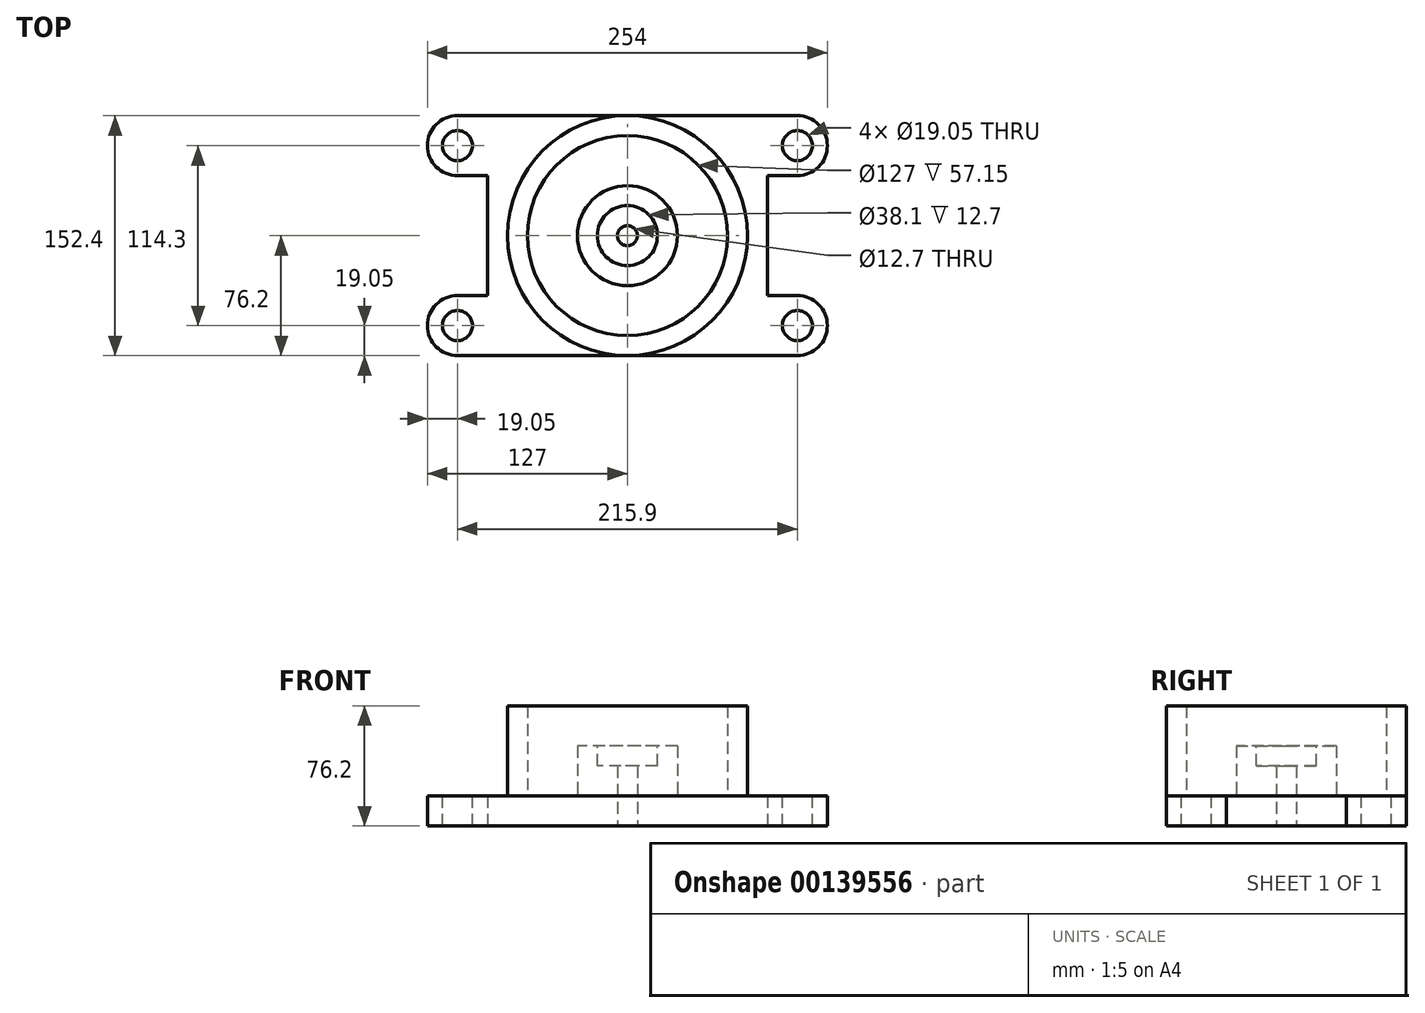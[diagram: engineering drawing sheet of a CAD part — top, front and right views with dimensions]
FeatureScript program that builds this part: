
annotation { "Feature Type Name" : "Feature", "Feature Type Description" : "" }
export const myFeature = defineFeature(function(context is Context, id is Id, definition is map)
    precondition{}
    {
        {
            var Q0;
            Q0=qCreatedBy(makeId("Top.planeOp"),FACE);
            var sketch = newSketch(context, id + "F0", { "sketchPlane" : qUnion([Q0])});
            skCircle(sketch, "E0", {"center": v(0, 0) * mm, "radius": 76.2 * mm});
            skCircle(sketch, "E1", {"center": v(0, 0) * mm, "radius": 63.5 * mm});
            skLineSegment(sketch, "E2", {"start": v(0, -76.2) * mm, "end": v(-127, -76.2) * mm});
            skLineSegment(sketch, "E3", {"start": v(-127, -76.2) * mm, "end": v(-127, -38.1) * mm});
            skLineSegment(sketch, "E4", {"start": v(-127, -38.1) * mm, "end": v(-88.9, -38.1) * mm});
            skLineSegment(sketch, "E5", {"start": v(0, 76.2) * mm, "end": v(0, -63.5) * mm, "construction": true});
            skLineSegment(sketch, "E6.MirrorCS", {"start": v(127, -38.1) * mm, "end": v(88.9, -38.1) * mm});
            skLineSegment(sketch, "E7.MirrorCS", {"start": v(0, -76.2) * mm, "end": v(127, -76.2) * mm});
            skLineSegment(sketch, "E8.MirrorCS", {"start": v(127, -76.2) * mm, "end": v(127, -38.1) * mm});
            skLineSegment(sketch, "E9", {"start": v(0, 76.2) * mm, "end": v(-127, 76.2) * mm});
            skLineSegment(sketch, "E10", {"start": v(0, 76.2) * mm, "end": v(127, 76.2) * mm});
            skLineSegment(sketch, "E11", {"start": v(-88.9, -38.1) * mm, "end": v(-88.9, 38.1) * mm});
            skLineSegment(sketch, "E12", {"start": v(127, 76.2) * mm, "end": v(127, 38.1) * mm});
            skLineSegment(sketch, "E13", {"start": v(127, 38.1) * mm, "end": v(88.9, 38.1) * mm});
            skLineSegment(sketch, "E14", {"start": v(88.9, -38.1) * mm, "end": v(88.9, 38.1) * mm});
            skLineSegment(sketch, "E15", {"start": v(-127, 76.2) * mm, "end": v(-127, 38.1) * mm});
            skLineSegment(sketch, "E16", {"start": v(-127, 38.1) * mm, "end": v(-88.9, 38.1) * mm});
            skLineSegment(sketch, "E17", {"start": v(0, 76.2) * mm, "end": v(0, -76.2) * mm, "construction": true});
            skCircle(sketch, "E18", {"center": v(0, 0) * mm, "radius": 31.75 * mm});
            skCircle(sketch, "E19", {"center": v(0, 0) * mm, "radius": 19.05 * mm});
            skCircle(sketch, "E20", {"center": v(0, 0) * mm, "radius": 6.35 * mm});
            skSolve(sketch);
        }
        {
            var Q0;
            Q0=makeQuery(id+"F0.imprint","IMPRINT",FACE,{"disambiguationData":[TD([[makeQuery(id+"F0.imprint","IMPRINT",EDGE,{"derivedFrom":sQuery(id+"F0.wireOp",EDGE,"E6.MirrorCS")}),1.0]])]});
            extrude(context, id + "F1", {"entities" : qUnion([Q0]), "depth" : 19.05 * mm});
        }
        {
            var Q0;
            Q0=makeQuery(id+"F0.imprint","IMPRINT",FACE,{"disambiguationData":[TD([[makeQuery(id+"F0.imprint","IMPRINT",EDGE,{"derivedFrom":sQuery(id+"F0.wireOp",EDGE,"E1")}),-1.0]])]});
            extrude(context, id + "F2", {"entities" : qUnion([Q0]), "operationType" : NewBodyOperationType.ADD, "depth" : 76.2 * mm});
        }
        {
            var Q0;
            Q0=makeQuery(id+"F0.imprint","IMPRINT",FACE,{"disambiguationData":[TD([[makeQuery(id+"F0.imprint","IMPRINT",EDGE,{"derivedFrom":sQuery(id+"F0.wireOp",EDGE,"E1")}),1.0]])]});
            extrude(context, id + "F3", {"entities" : qUnion([Q0]), "operationType" : NewBodyOperationType.ADD, "depth" : 19.05 * mm});
        }
        {
            var Q0;
            Q0=makeQuery(id+"F0.imprint","IMPRINT",FACE,{"disambiguationData":[TD([[makeQuery(id+"F0.imprint","IMPRINT",EDGE,{"derivedFrom":sQuery(id+"F0.wireOp",EDGE,"E18")}),1.0]])]});
            var Q1;
            Q1=makeQuery(id+"F0.imprint","IMPRINT",FACE,{"disambiguationData":[TD([[makeQuery(id+"F0.imprint","IMPRINT",EDGE,{"derivedFrom":sQuery(id+"F0.wireOp",EDGE,"E19")}),1.0]])]});
            var Q2;
            Q2=makeQuery(id+"F0.imprint","IMPRINT",FACE,{"disambiguationData":[TD([[makeQuery(id+"F0.imprint","IMPRINT",EDGE,{"derivedFrom":sQuery(id+"F0.wireOp",EDGE,"E20")}),1.0]])]});
            extrude(context, id + "F4", {"entities" : qUnion([Q0, Q1, Q2]), "operationType" : NewBodyOperationType.ADD, "depth" : 50.8 * mm});
        }
        {
            var Q0;
            Q0=makeQuery(id+"F4.opExtrude","CAP_FACE",FACE,{"disambiguationData":[OSD([sQuery(id+"F0.wireOp",EDGE,"E18")])],"isStart":false});
            var sketch = newSketch(context, id + "F5", { "sketchPlane" : qUnion([Q0])});
            skCircle(sketch, "E21.0", {"center": v(0, 0) * mm, "radius": 19.05 * mm});
            skSolve(sketch);
        }
        {
            var Q0;
            Q0=qSketchRegion(id+"F5",true);
            extrude(context, id + "F6", {"entities" : qUnion([Q0]), "operationType" : NewBodyOperationType.REMOVE, "oppositeDirection" : true, "depth" : 12.7 * mm});
        }
        {
            var Q0;
            Q0=makeQuery(id+"F0.imprint","IMPRINT",FACE,{"disambiguationData":[TD([[makeQuery(id+"F0.imprint","IMPRINT",EDGE,{"derivedFrom":sQuery(id+"F0.wireOp",EDGE,"E20")}),1.0]])]});
            extrude(context, id + "F7", {"entities" : qUnion([Q0]), "operationType" : NewBodyOperationType.REMOVE, "endBound" : BoundingType.THROUGH_ALL, "depth" : 25.4 * mm});
        }
        {
            var Q0;
            {var subQ0=sQuery(id+"F0.wireOp",EDGE,"E2");Q0=makeQuery(id+"F0.imprint","IMPRINT",FACE,{"disambiguationData":[TD([[makeQuery(id+"F0.imprint","IMPRINT",EDGE,{"derivedFrom":subQ0}),-1.0]])]});}
            extrude(context, id + "F8", {"entities" : qUnion([Q0]), "operationType" : NewBodyOperationType.ADD, "depth" : 19.05 * mm});
        }
        {
            var Q0;
            Q0=makeQuery(id+"F8.opExtrude","SWEPT_EDGE",EDGE,{"disambiguationData":[OSD([sQuery(id+"F0.wireOp",EDGE,"E2"),sQuery(id+"F0.wireOp",EDGE,"E3")])]});
            var Q1;
            Q1=makeQuery(id+"F8.opExtrude","SWEPT_EDGE",EDGE,{"disambiguationData":[OSD([sQuery(id+"F0.wireOp",EDGE,"E3"),sQuery(id+"F0.wireOp",EDGE,"E4")])]});
            var Q2;
            Q2=makeQuery(id+"F8.opExtrude","SWEPT_EDGE",EDGE,{"disambiguationData":[OSD([sQuery(id+"F0.wireOp",EDGE,"E15"),sQuery(id+"F0.wireOp",EDGE,"E16")])]});
            var Q3;
            Q3=makeQuery(id+"F8.opExtrude","SWEPT_EDGE",EDGE,{"disambiguationData":[OSD([sQuery(id+"F0.wireOp",EDGE,"E9"),sQuery(id+"F0.wireOp",EDGE,"E15")])]});
            var Q4;
            Q4=makeQuery(id+"F1.opExtrude","SWEPT_EDGE",EDGE,{"disambiguationData":[OSD([sQuery(id+"F0.wireOp",EDGE,"E12"),sQuery(id+"F0.wireOp",EDGE,"E13")])]});
            var Q5;
            Q5=makeQuery(id+"F1.opExtrude","SWEPT_EDGE",EDGE,{"disambiguationData":[OSD([sQuery(id+"F0.wireOp",EDGE,"E10"),sQuery(id+"F0.wireOp",EDGE,"E12")])]});
            var Q6;
            Q6=makeQuery(id+"F1.opExtrude","SWEPT_EDGE",EDGE,{"disambiguationData":[OSD([sQuery(id+"F0.wireOp",EDGE,"E7.MirrorCS"),sQuery(id+"F0.wireOp",EDGE,"E8.MirrorCS")])]});
            var Q7;
            Q7=makeQuery(id+"F1.opExtrude","SWEPT_EDGE",EDGE,{"disambiguationData":[OSD([sQuery(id+"F0.wireOp",EDGE,"E6.MirrorCS"),sQuery(id+"F0.wireOp",EDGE,"E8.MirrorCS")])]});
            fillet(context, id + "F9", {"entities" : qUnion([Q0, Q1, Q2, Q3, Q4, Q5, Q6, Q7]), "radius" : 19.05 * mm, "tangentPropagation" : true, "allowEdgeOverflow" : false});
        }
        {
            var Q0;
            Q0=makeQuery(id+"F8.opExtrude","CAP_FACE",FACE,{"disambiguationData":[OSD([sQuery(id+"F0.wireOp",EDGE,"E0"),sQuery(id+"F0.wireOp",EDGE,"E2"),sQuery(id+"F0.wireOp",EDGE,"E3"),sQuery(id+"F0.wireOp",EDGE,"E4"),sQuery(id+"F0.wireOp",EDGE,"E9"),sQuery(id+"F0.wireOp",EDGE,"E11"),sQuery(id+"F0.wireOp",EDGE,"E15"),sQuery(id+"F0.wireOp",EDGE,"E16")])],"isStart":false});
            var sketch = newSketch(context, id + "F10", { "sketchPlane" : qUnion([Q0])});
            skArc(sketch, "E22.0", {"start": v(-107.95, 76.2) * mm, "mid": v(-127, 57.15) * mm, "end": v(-107.95, 38.1) * mm});
            skArc(sketch, "E23.0", {"start": v(-107.95, -38.1) * mm, "mid": v(-127, -57.15) * mm, "end": v(-107.95, -76.2) * mm});
            skCircle(sketch, "E24", {"center": v(-107.95, -57.15) * mm, "radius": 9.53 * mm});
            skCircle(sketch, "E25", {"center": v(-107.95, 57.15) * mm, "radius": 9.53 * mm});
            skLineSegment(sketch, "E26.0", {"start": v(0, 76.2) * mm, "end": v(0, -63.5) * mm});
            skCircle(sketch, "E27.MirrorC", {"center": v(107.95, 57.15) * mm, "radius": 9.53 * mm});
            skCircle(sketch, "E28.MirrorC", {"center": v(107.95, -57.15) * mm, "radius": 9.53 * mm});
            skSolve(sketch);
        }
        {
            var Q0;
            Q0=qSketchRegion(id+"F10",true);
            var Q1;
            {var subQ0=sQuery(id+"F0.wireOp",EDGE,"E0");var subQ1=sQuery(id+"F0.wireOp",EDGE,"E18");var subQ2=sQuery(id+"F0.wireOp",EDGE,"E1");Q1=makeQuery(id+"F8.boolean.opBoolean","MERGE",FACE,{"derivedFrom":[makeQuery(id+"F4.boolean.opBoolean","MERGE",FACE,{"derivedFrom":[makeQuery(id+"F3.boolean.opBoolean","MERGE",FACE,{"derivedFrom":[makeQuery(id+"F2.boolean.opBoolean","MERGE",FACE,{"derivedFrom":[makeQuery(id+"F1.opExtrude","CAP_FACE",FACE,{"disambiguationData":[OSD([subQ0,sQuery(id+"F0.wireOp",EDGE,"E6.MirrorCS"),sQuery(id+"F0.wireOp",EDGE,"E7.MirrorCS"),sQuery(id+"F0.wireOp",EDGE,"E8.MirrorCS"),sQuery(id+"F0.wireOp",EDGE,"E10"),sQuery(id+"F0.wireOp",EDGE,"E12"),sQuery(id+"F0.wireOp",EDGE,"E13"),sQuery(id+"F0.wireOp",EDGE,"E14")])],"isStart":true}),makeQuery(id+"F2.opExtrude","CAP_FACE",FACE,{"disambiguationData":[OSD([subQ0,subQ2])],"isStart":true})]}),makeQuery(id+"F3.opExtrude","CAP_FACE",FACE,{"disambiguationData":[OSD([subQ2,subQ1])],"isStart":true})]}),makeQuery(id+"F4.opExtrude","CAP_FACE",FACE,{"disambiguationData":[OSD([subQ1])],"isStart":true})]}),makeQuery(id+"F8.opExtrude","CAP_FACE",FACE,{"disambiguationData":[OSD([subQ0,sQuery(id+"F0.wireOp",EDGE,"E2"),sQuery(id+"F0.wireOp",EDGE,"E3"),sQuery(id+"F0.wireOp",EDGE,"E4"),sQuery(id+"F0.wireOp",EDGE,"E9"),sQuery(id+"F0.wireOp",EDGE,"E11"),sQuery(id+"F0.wireOp",EDGE,"E15"),sQuery(id+"F0.wireOp",EDGE,"E16")])],"isStart":true})]});}
            extrude(context, id + "F11", {"entities" : qUnion([Q0]), "operationType" : NewBodyOperationType.REMOVE, "endBound" : BoundingType.UP_TO_SURFACE, "oppositeDirection" : true, "endBoundEntityFace" : qUnion([Q1]), "depth" : 25.4 * mm});
        }
    });
